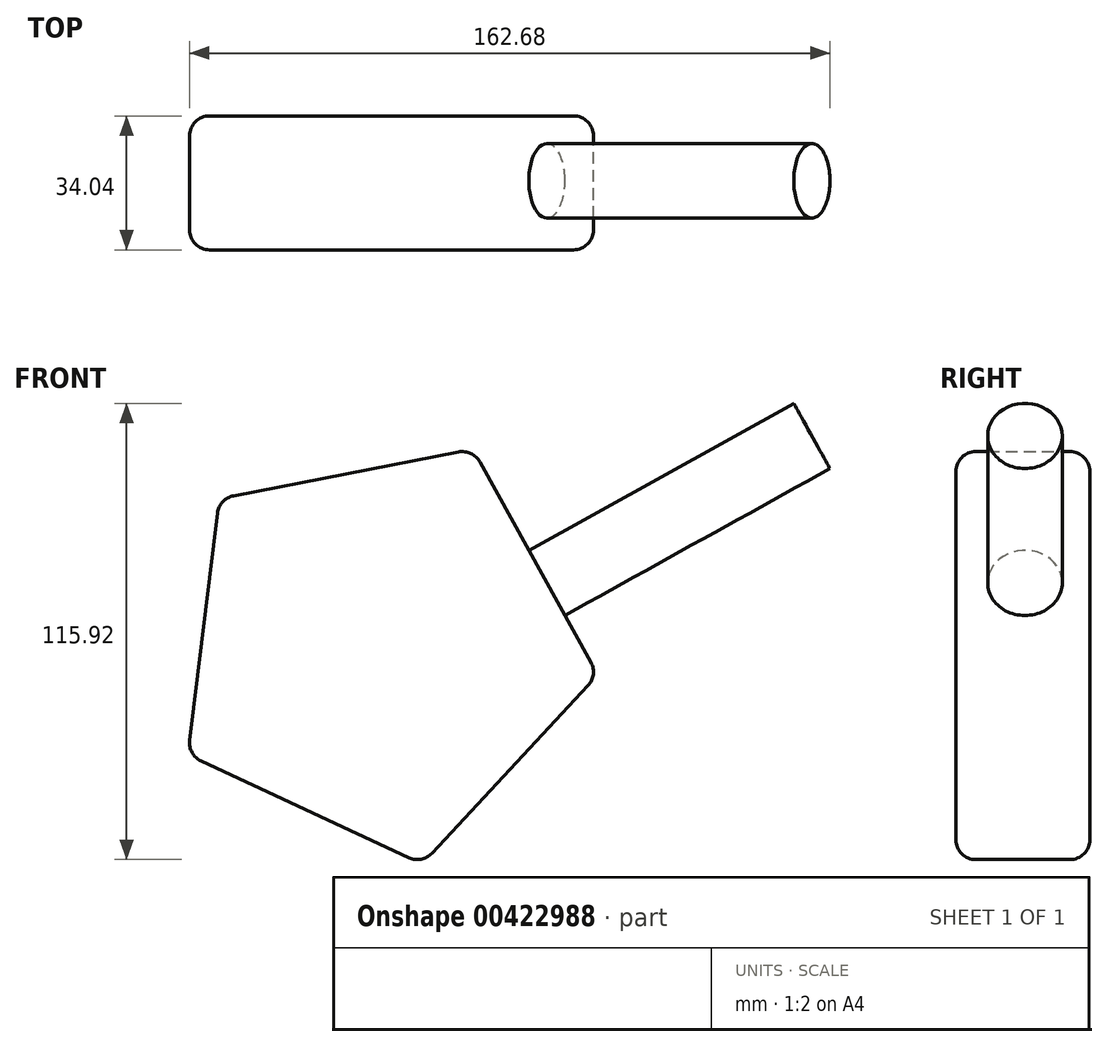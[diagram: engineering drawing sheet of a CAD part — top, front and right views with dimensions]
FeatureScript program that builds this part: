
annotation { "Feature Type Name" : "Feature", "Feature Type Description" : "" }
export const myFeature = defineFeature(function(context is Context, id is Id, definition is map)
    precondition{}
    {
        {
            var Q0;
            Q0=qCreatedBy(makeId("Front.planeOp"),FACE);
            var sketch = newSketch(context, id + "F0", { "sketchPlane" : qUnion([Q0])});
            skCircle(sketch, "E0.cCircle", {"center": v(0, 0) * mm, "radius": 45.14 * mm, "construction": true});
            skLineSegment(sketch, "E0.0", {"start": v(23.57, 50.58) * mm, "end": v(55.39, -6.78) * mm});
            skLineSegment(sketch, "E0.1", {"start": v(55.39, -6.78) * mm, "end": v(10.67, -54.77) * mm});
            skLineSegment(sketch, "E0.2", {"start": v(10.67, -54.77) * mm, "end": v(-48.8, -27.07) * mm});
            skLineSegment(sketch, "E0.3", {"start": v(-48.8, -27.07) * mm, "end": v(-40.82, 38.04) * mm});
            skLineSegment(sketch, "E0.4", {"start": v(-40.82, 38.04) * mm, "end": v(23.57, 50.58) * mm});
            skPoint(sketch, "E0.0.midPoint", {"position": v(39.48, 21.9) * mm});
            skSolve(sketch);
        }
        {
            var Q0;
            Q0 = qSketchRegion(id + "F0", true);
            extrude(context, id + "F1", {"entities" : qUnion([Q0]), "depth" : 34.04 * mm, "offsetDistance" : 25.4 * mm});
        }
        {
            var Q0;
            Q0=makeQuery(id+"F1.opExtrude","SWEPT_FACE",FACE,{"disambiguationData":[OSD([sQuery(id+"F0.wireOp",EDGE,"E0.0")])]});
            var sketch = newSketch(context, id + "F2", { "sketchPlane" : qUnion([Q0])});
            skCircle(sketch, "E1", {"center": v(-16.48, -6.04) * mm, "radius": 9.47 * mm});
            skSolve(sketch);
        }
        {
            var Q0;
            Q0 = qSketchRegion(id + "F2", true);
            extrude(context, id + "F3", {"entities" : qUnion([Q0]), "operationType" : NewBodyOperationType.ADD, "depth" : 76.96 * mm, "offsetDistance" : 25.4 * mm});
        }
        {
            var Q0;
            Q0=makeQuery(id+"F1.opExtrude","CAP_EDGE",EDGE,{"disambiguationData":[OSD([sQuery(id+"F0.wireOp",EDGE,"E0.0")])],"isStart":true});
            var Q1;
            Q1=makeQuery(id+"F1.opExtrude","SWEPT_EDGE",EDGE,{"disambiguationData":[OSD([sQuery(id+"F0.wireOp",EDGE,"E0.0"),sQuery(id+"F0.wireOp",EDGE,"E0.1")])]});
            var Q2;
            Q2=makeQuery(id+"F1.opExtrude","SWEPT_EDGE",EDGE,{"disambiguationData":[OSD([sQuery(id+"F0.wireOp",EDGE,"E0.0"),sQuery(id+"F0.wireOp",EDGE,"E0.4")])]});
            var Q3;
            Q3=makeQuery(id+"F1.opExtrude","CAP_EDGE",EDGE,{"disambiguationData":[OSD([sQuery(id+"F0.wireOp",EDGE,"E0.0")])],"isStart":false});
            var Q4;
            Q4=makeQuery(id+"F1.opExtrude","CAP_EDGE",EDGE,{"disambiguationData":[OSD([sQuery(id+"F0.wireOp",EDGE,"E0.1")])],"isStart":false});
            var Q5;
            Q5=makeQuery(id+"F1.opExtrude","SWEPT_EDGE",EDGE,{"disambiguationData":[OSD([sQuery(id+"F0.wireOp",EDGE,"E0.1"),sQuery(id+"F0.wireOp",EDGE,"E0.2")])]});
            var Q6;
            Q6=makeQuery(id+"F1.opExtrude","CAP_EDGE",EDGE,{"disambiguationData":[OSD([sQuery(id+"F0.wireOp",EDGE,"E0.1")])],"isStart":true});
            var Q7;
            Q7=makeQuery(id+"F1.opExtrude","CAP_EDGE",EDGE,{"disambiguationData":[OSD([sQuery(id+"F0.wireOp",EDGE,"E0.4")])],"isStart":true});
            var Q8;
            Q8=makeQuery(id+"F1.opExtrude","CAP_EDGE",EDGE,{"disambiguationData":[OSD([sQuery(id+"F0.wireOp",EDGE,"E0.4")])],"isStart":false});
            var Q9;
            Q9=makeQuery(id+"F1.opExtrude","CAP_EDGE",EDGE,{"disambiguationData":[OSD([sQuery(id+"F0.wireOp",EDGE,"E0.3")])],"isStart":false});
            var Q10;
            Q10=makeQuery(id+"F1.opExtrude","CAP_EDGE",EDGE,{"disambiguationData":[OSD([sQuery(id+"F0.wireOp",EDGE,"E0.2")])],"isStart":false});
            var Q11;
            Q11=makeQuery(id+"F1.opExtrude","SWEPT_EDGE",EDGE,{"disambiguationData":[OSD([sQuery(id+"F0.wireOp",EDGE,"E0.3"),sQuery(id+"F0.wireOp",EDGE,"E0.4")])]});
            var Q12;
            Q12=makeQuery(id+"F1.opExtrude","SWEPT_EDGE",EDGE,{"disambiguationData":[OSD([sQuery(id+"F0.wireOp",EDGE,"E0.2"),sQuery(id+"F0.wireOp",EDGE,"E0.3")])]});
            var Q13;
            Q13=makeQuery(id+"F1.opExtrude","CAP_EDGE",EDGE,{"disambiguationData":[OSD([sQuery(id+"F0.wireOp",EDGE,"E0.3")])],"isStart":true});
            var Q14;
            Q14=makeQuery(id+"F1.opExtrude","CAP_EDGE",EDGE,{"disambiguationData":[OSD([sQuery(id+"F0.wireOp",EDGE,"E0.2")])],"isStart":true});
            fillet(context, id + "F4", {"entities" : qUnion([Q0, Q1, Q2, Q3, Q4, Q5, Q6, Q7, Q8, Q9, Q10, Q11, Q12, Q13, Q14]), "radius" : 5.08 * mm, "tangentPropagation" : true, "allowEdgeOverflow" : false});
        }
    });
